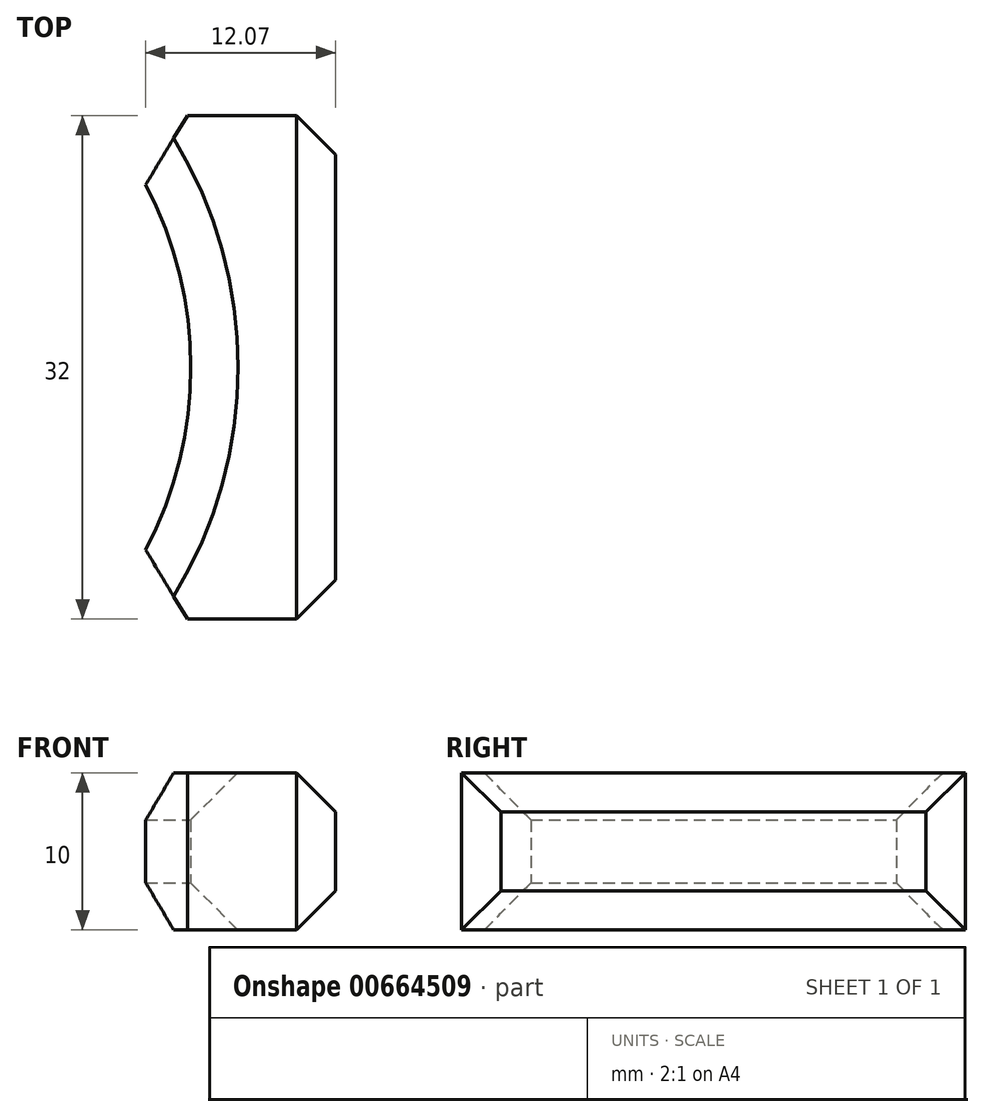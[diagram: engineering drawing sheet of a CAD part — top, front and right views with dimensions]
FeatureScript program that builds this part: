
annotation { "Feature Type Name" : "Feature", "Feature Type Description" : "" }
export const myFeature = defineFeature(function(context is Context, id is Id, definition is map)
    precondition{}
    {
        {
            var Q0;
            Q0=qCreatedBy(makeId("Top.planeOp"),FACE);
            var sketch = newSketch(context, id + "F0", { "sketchPlane" : qUnion([Q0])});
            skLineSegment(sketch, "E0.bottom", {"start": v(7.5, -16) * mm, "end": v(-7.5, -16) * mm});
            skLineSegment(sketch, "E0.top", {"start": v(7.5, 16) * mm, "end": v(-7.5, 16) * mm});
            skLineSegment(sketch, "E0.left", {"start": v(7.5, -16) * mm, "end": v(7.5, 16) * mm});
            skLineSegment(sketch, "E0.right", {"start": v(-7.5, -16) * mm, "end": v(-7.5, 16) * mm});
            skPoint(sketch, "E0.middle", {"position": v(0, 0) * mm});
            skArc(sketch, "E1", {"start": v(-7.5, -16) * mm, "mid": v(-1.7, 0) * mm, "end": v(-7.5, 16) * mm});
            skPoint(sketch, "E1.third.point", {"position": v(-51.7, 0) * mm});
            skLineSegment(sketch, "E2", {"start": v(-7.5, 0) * mm, "end": v(-26.7, 0) * mm});
            skSolve(sketch);
        }
        {
            var Q0;
            Q0=makeQuery(id+"F0.imprint","IMPRINT",FACE,{"disambiguationData":[TD([[makeQuery(id+"F0.imprint","IMPRINT",EDGE,{"derivedFrom":sQuery(id+"F0.wireOp",EDGE,"E0.bottom")}),-1.0]])]});
            extrude(context, id + "F1", {"entities" : qUnion([Q0]), "depth" : 10 * mm, "offsetDistance" : 25 * mm});
        }
        {
            var Q0;
            Q0=makeQuery(id+"F1.opExtrude","SWEPT_FACE",FACE,{"disambiguationData":[OSD([sQuery(id+"F0.wireOp",EDGE,"E0.left")])]});
            chamfer(context, id + "F2", {"entities" : qUnion([Q0]), "width" : 2.5 * mm, "tangentPropagation" : true});
        }
        {
            var Q0;
            Q0=makeQuery(id+"F1.opExtrude","SWEPT_FACE",FACE,{"disambiguationData":[OSD([sQuery(id+"F0.wireOp",EDGE,"E1")])]});
            chamfer(context, id + "F3", {"entities" : qUnion([Q0]), "width" : 3 * mm, "tangentPropagation" : true});
        }
    });
